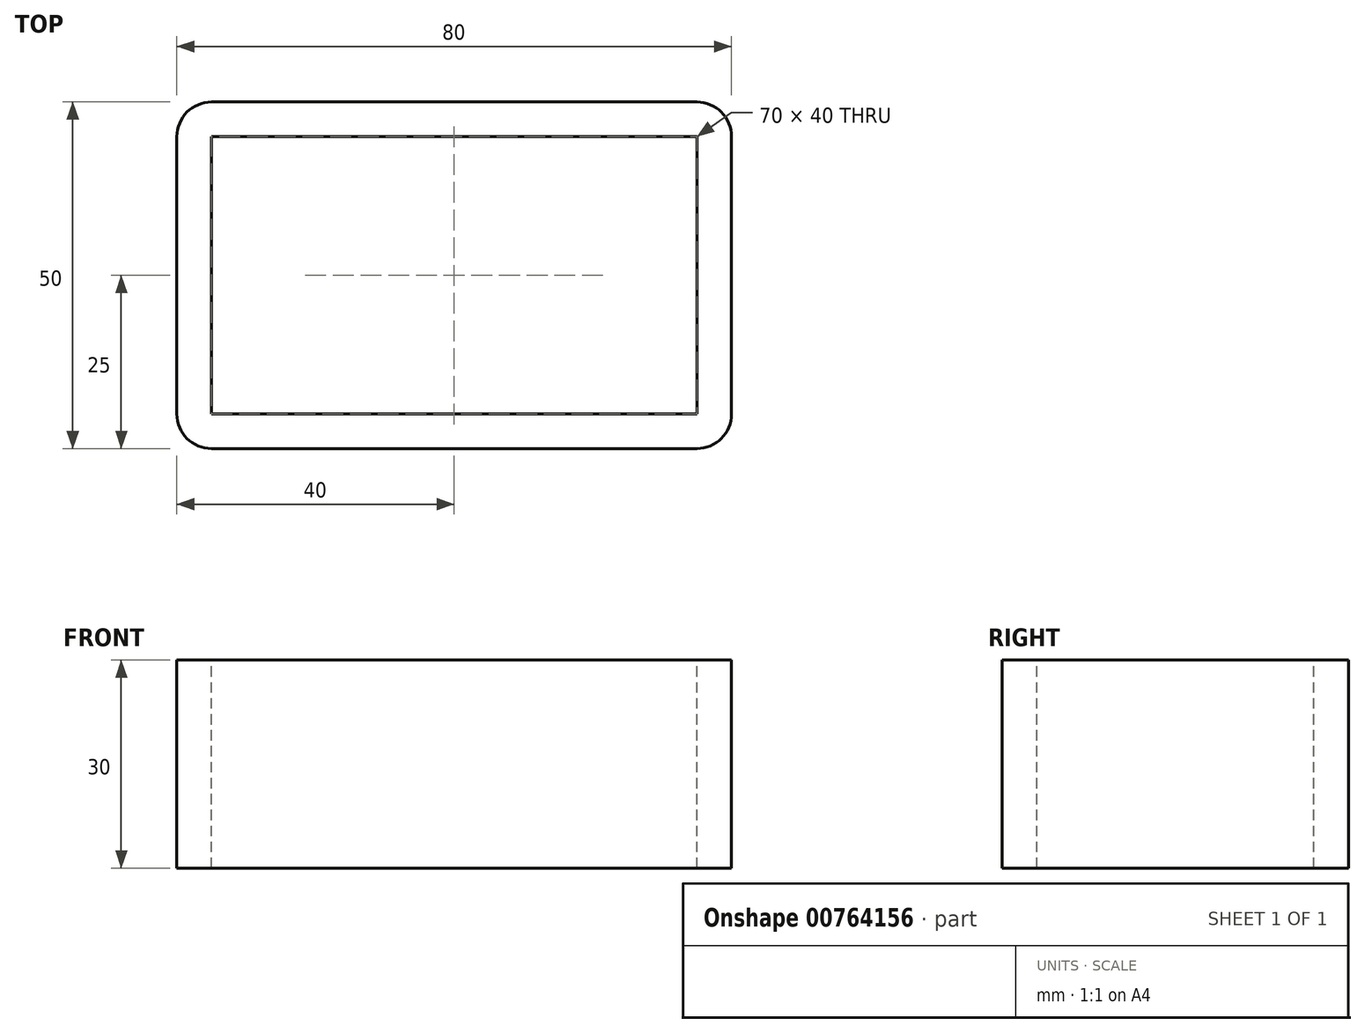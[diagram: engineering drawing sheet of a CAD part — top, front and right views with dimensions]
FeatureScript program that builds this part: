
annotation { "Feature Type Name" : "Feature", "Feature Type Description" : "" }
export const myFeature = defineFeature(function(context is Context, id is Id, definition is map)
    precondition{}
    {
        {
            var Q0;
            Q0=qCreatedBy(makeId("Top.planeOp"),FACE);
            var sketch = newSketch(context, id + "F0", { "sketchPlane" : qUnion([Q0])});
            skLineSegment(sketch, "E0.bottom", {"start": v(0, 0) * mm, "end": v(80, 0) * mm});
            skLineSegment(sketch, "E0.top", {"start": v(0, 50) * mm, "end": v(80, 50) * mm});
            skLineSegment(sketch, "E0.left", {"start": v(0, 0) * mm, "end": v(0, 50) * mm});
            skLineSegment(sketch, "E0.right", {"start": v(80, 0) * mm, "end": v(80, 50) * mm});
            skSolve(sketch);
        }
        {
            var Q0;
            Q0 = qSketchRegion(id + "F0", true);
            extrude(context, id + "F1", {"entities" : qUnion([Q0]), "depth" : 30 * mm, "offsetDistance" : 25 * mm});
        }
        {
            var Q0;
            Q0=makeQuery(id+"F1.opExtrude","CAP_FACE",FACE,{"disambiguationData":[OSD([sQuery(id+"F0.wireOp",EDGE,"E0.bottom"),sQuery(id+"F0.wireOp",EDGE,"E0.top"),sQuery(id+"F0.wireOp",EDGE,"E0.left"),sQuery(id+"F0.wireOp",EDGE,"E0.right")])],"isStart":false});
            var sketch = newSketch(context, id + "F2", { "sketchPlane" : qUnion([Q0])});
            skLineSegment(sketch, "E1.0", {"start": v(5, 45) * mm, "end": v(75, 45) * mm});
            skLineSegment(sketch, "E1.1", {"start": v(5, 5) * mm, "end": v(5, 45) * mm});
            skLineSegment(sketch, "E1.2", {"start": v(5, 5) * mm, "end": v(75, 5) * mm});
            skLineSegment(sketch, "E1.3", {"start": v(75, 5) * mm, "end": v(75, 45) * mm});
            skSolve(sketch);
        }
        {
            var Q0;
            Q0 = qSketchRegion(id + "F2", true);
            extrude(context, id + "F3", {"entities" : qUnion([Q0]), "operationType" : NewBodyOperationType.REMOVE, "endBound" : BoundingType.THROUGH_ALL, "oppositeDirection" : true, "depth" : 49.4 * mm, "offsetDistance" : 25 * mm});
        }
        {
            var Q0;
            Q0=makeQuery(id+"F1.opExtrude","SWEPT_EDGE",EDGE,{"disambiguationData":[OSD([sQuery(id+"F0.wireOp",EDGE,"E0.bottom"),sQuery(id+"F0.wireOp",EDGE,"E0.left")])]});
            var Q1;
            Q1=makeQuery(id+"F1.opExtrude","SWEPT_EDGE",EDGE,{"disambiguationData":[OSD([sQuery(id+"F0.wireOp",EDGE,"E0.bottom"),sQuery(id+"F0.wireOp",EDGE,"E0.right")])]});
            var Q2;
            Q2=makeQuery(id+"F1.opExtrude","SWEPT_EDGE",EDGE,{"disambiguationData":[OSD([sQuery(id+"F0.wireOp",EDGE,"E0.top"),sQuery(id+"F0.wireOp",EDGE,"E0.left")])]});
            var Q3;
            Q3=makeQuery(id+"F1.opExtrude","SWEPT_EDGE",EDGE,{"disambiguationData":[OSD([sQuery(id+"F0.wireOp",EDGE,"E0.top"),sQuery(id+"F0.wireOp",EDGE,"E0.right")])]});
            fillet(context, id + "F4", {"entities" : qUnion([Q0, Q1, Q2, Q3]), "radius" : 5 * mm, "tangentPropagation" : true, "allowEdgeOverflow" : false});
        }
    });
